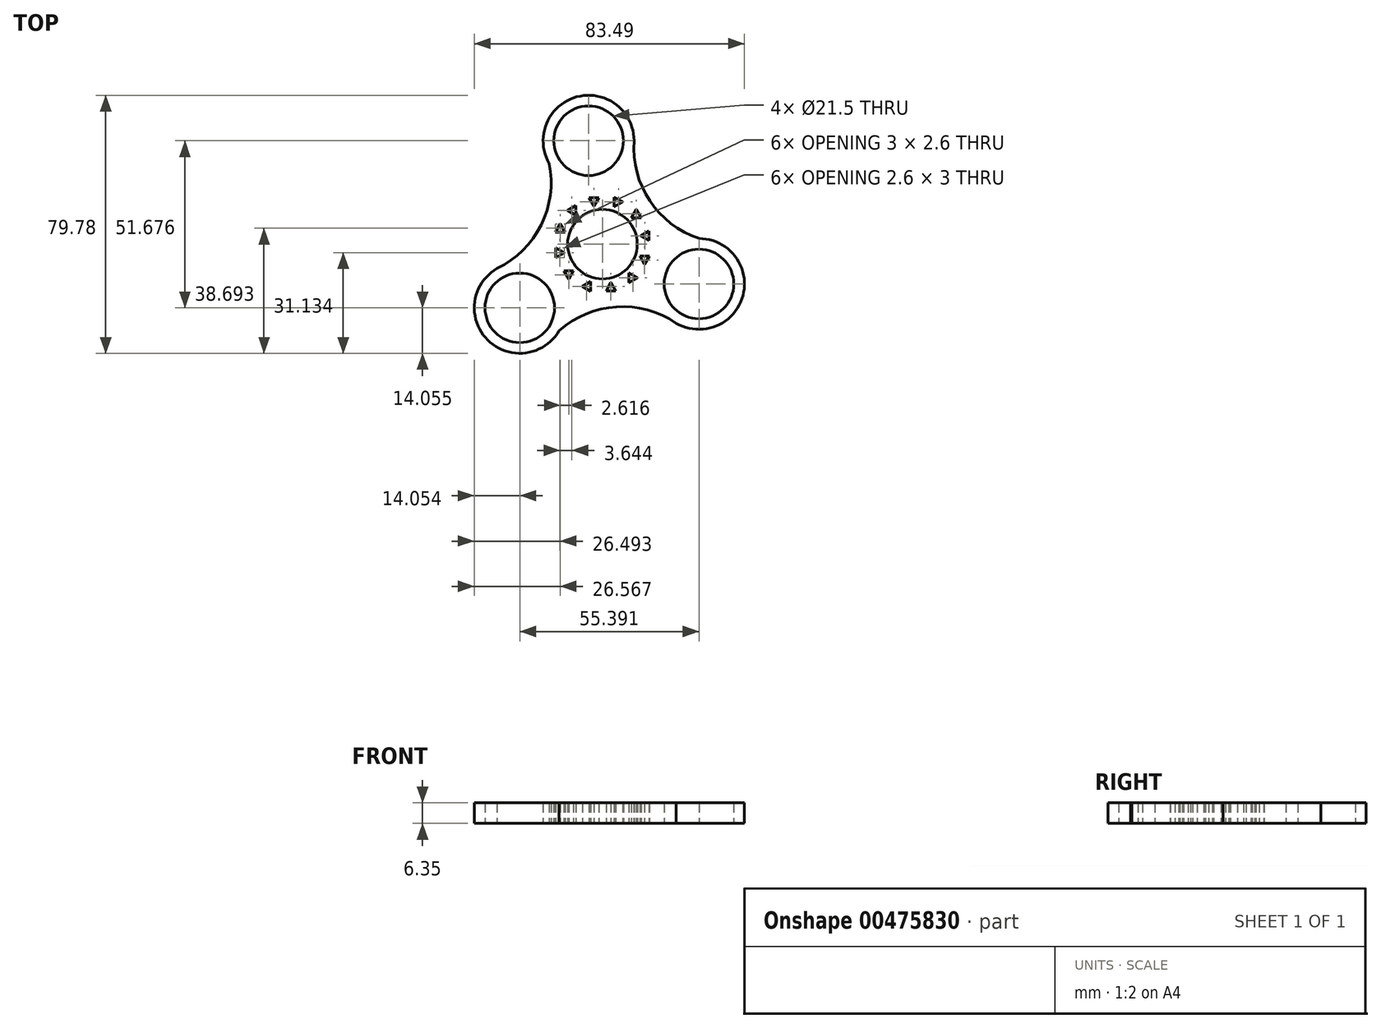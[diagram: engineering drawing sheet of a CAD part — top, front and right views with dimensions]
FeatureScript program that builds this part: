
annotation { "Feature Type Name" : "Feature", "Feature Type Description" : "" }
export const myFeature = defineFeature(function(context is Context, id is Id, definition is map)
    precondition{}
    {
        {
            var Q0;
            Q0=qCreatedBy(makeId("Top.planeOp"),FACE);
            var sketch = newSketch(context, id + "F0", { "sketchPlane" : qUnion([Q0])});
            skCircle(sketch, "E0", {"center": v(0, 0) * mm, "radius": 10.75 * mm});
            skArc(sketch, "E1", {"start": v(-31.32, -6.88) * mm, "mid": v(-35.98, -29.12) * mm, "end": v(-13.39, -26.72) * mm});
            skCircle(sketch, "E2", {"center": v(-25.56, -19.7) * mm, "radius": 10.75 * mm});
            skArc(sketch, "E3.1.2", {"start": v(21.62, -23.68) * mm, "mid": v(43.2, -16.6) * mm, "end": v(29.83, 1.77) * mm});
            skCircle(sketch, "E3.1.3", {"center": v(29.83, -12.28) * mm, "radius": 10.75 * mm});
            skArc(sketch, "E3.2.2", {"start": v(9.7, 30.56) * mm, "mid": v(-7.22, 45.72) * mm, "end": v(-16.45, 24.96) * mm});
            skCircle(sketch, "E3.2.3", {"center": v(-4.28, 31.98) * mm, "radius": 10.75 * mm});
            skArc(sketch, "E4", {"start": v(9.77, 31.98) * mm, "mid": v(14.62, 13.43) * mm, "end": v(29.83, 1.77) * mm});
            skArc(sketch, "E5.1.0", {"start": v(-32.58, -7.53) * mm, "mid": v(-18.94, 5.95) * mm, "end": v(-16.45, 24.96) * mm});
            skArc(sketch, "E5.2.0", {"start": v(22.8, -24.45) * mm, "mid": v(4.32, -19.38) * mm, "end": v(-13.39, -26.72) * mm});
            skLineSegment(sketch, "E6", {"start": v(-15.18, -6.28) * mm, "end": v(-10.43, -2.62) * mm});
            skLineSegment(sketch, "E7.MirrorCS", {"start": v(-9.8, -13.27) * mm, "end": v(-5.04, -9.6) * mm});
            skLineSegment(sketch, "E8.1.0", {"start": v(19.09, -12.43) * mm, "end": v(19.08, -12.43) * mm});
            skLineSegment(sketch, "E8.1.1", {"start": v(22.6, -4.34) * mm, "end": v(22.44, -4.28) * mm});
            skLineSegment(sketch, "E8.2.0", {"start": v(1.67, 23.03) * mm, "end": v(1.73, 22.6) * mm});
            skLineSegment(sketch, "E8.2.1", {"start": v(-7.04, 21.6) * mm, "end": v(-7.02, 21.43) * mm});
            skPoint(sketch, "E8.center", {"position": v(0.3, 0.07) * mm});
            skArc(sketch, "E9", {"start": v(-15.18, -6.28) * mm, "mid": v(-12.99, -10.16) * mm, "end": v(-9.8, -13.27) * mm});
            skArc(sketch, "E10.1.0", {"start": v(13.53, -10.15) * mm, "mid": v(15.8, -6.31) * mm, "end": v(16.9, -2) * mm});
            skArc(sketch, "E10.2.0", {"start": v(2.52, 16.65) * mm, "mid": v(-1.93, 16.7) * mm, "end": v(-6.22, 15.48) * mm});
            skLineSegment(sketch, "E11.trimOffspring", {"start": v(16.9, -2) * mm, "end": v(11.34, 0.3) * mm});
            skLineSegment(sketch, "E12.trimOffspring", {"start": v(13.53, -10.15) * mm, "end": v(7.98, -7.86) * mm});
            skLineSegment(sketch, "E13.trimOffspring", {"start": v(2.52, 16.65) * mm, "end": v(3.32, 10.7) * mm});
            skLineSegment(sketch, "E14.trimOffspring", {"start": v(-6.22, 15.48) * mm, "end": v(-5.42, 9.53) * mm});
            skLineSegment(sketch, "E15", {"start": v(-14.54, 3.64) * mm, "end": v(-13.04, 6.24) * mm});
            skLineSegment(sketch, "E16", {"start": v(-13.04, 6.24) * mm, "end": v(-11.54, 3.64) * mm});
            skLineSegment(sketch, "E17", {"start": v(-11.54, 3.64) * mm, "end": v(-14.54, 3.64) * mm});
            skLineSegment(sketch, "E18.1.0", {"start": v(-14.42, -4.12) * mm, "end": v(-14.42, -1.12) * mm});
            skLineSegment(sketch, "E18.1.1", {"start": v(-14.42, -1.12) * mm, "end": v(-11.82, -2.62) * mm});
            skLineSegment(sketch, "E18.1.2", {"start": v(-11.82, -2.62) * mm, "end": v(-14.42, -4.12) * mm});
            skLineSegment(sketch, "E18.2.0", {"start": v(-10.43, -10.77) * mm, "end": v(-11.93, -8.17) * mm});
            skLineSegment(sketch, "E18.2.1", {"start": v(-11.93, -8.17) * mm, "end": v(-8.93, -8.17) * mm});
            skLineSegment(sketch, "E18.2.2", {"start": v(-8.93, -8.17) * mm, "end": v(-10.43, -10.77) * mm});
            skLineSegment(sketch, "E19.1.3.0", {"start": v(-3.64, -14.54) * mm, "end": v(-6.24, -13.04) * mm});
            skLineSegment(sketch, "E19.3.3.0", {"start": v(-6.24, -13.04) * mm, "end": v(-3.64, -11.54) * mm});
            skLineSegment(sketch, "E19.6.3.0", {"start": v(-3.64, -11.54) * mm, "end": v(-3.64, -14.54) * mm});
            skLineSegment(sketch, "E19.1.4.0", {"start": v(4.12, -14.42) * mm, "end": v(1.12, -14.42) * mm});
            skLineSegment(sketch, "E19.3.4.0", {"start": v(1.12, -14.42) * mm, "end": v(2.62, -11.82) * mm});
            skLineSegment(sketch, "E19.6.4.0", {"start": v(2.62, -11.82) * mm, "end": v(4.12, -14.42) * mm});
            skLineSegment(sketch, "E19.1.5.0", {"start": v(10.77, -10.43) * mm, "end": v(8.17, -11.93) * mm});
            skLineSegment(sketch, "E19.3.5.0", {"start": v(8.17, -11.93) * mm, "end": v(8.17, -8.93) * mm});
            skLineSegment(sketch, "E19.6.5.0", {"start": v(8.17, -8.93) * mm, "end": v(10.77, -10.43) * mm});
            skLineSegment(sketch, "E20.1.6.0", {"start": v(14.54, -3.64) * mm, "end": v(13.04, -6.24) * mm});
            skLineSegment(sketch, "E20.3.6.0", {"start": v(13.04, -6.24) * mm, "end": v(11.54, -3.64) * mm});
            skLineSegment(sketch, "E20.6.6.0", {"start": v(11.54, -3.64) * mm, "end": v(14.54, -3.64) * mm});
            skLineSegment(sketch, "E20.1.7.0", {"start": v(14.42, 4.12) * mm, "end": v(14.42, 1.12) * mm});
            skLineSegment(sketch, "E20.3.7.0", {"start": v(14.42, 1.12) * mm, "end": v(11.82, 2.62) * mm});
            skLineSegment(sketch, "E20.6.7.0", {"start": v(11.82, 2.62) * mm, "end": v(14.42, 4.12) * mm});
            skLineSegment(sketch, "E20.1.8.0", {"start": v(10.43, 10.77) * mm, "end": v(11.93, 8.17) * mm});
            skLineSegment(sketch, "E20.3.8.0", {"start": v(11.93, 8.17) * mm, "end": v(8.93, 8.17) * mm});
            skLineSegment(sketch, "E20.6.8.0", {"start": v(8.93, 8.17) * mm, "end": v(10.43, 10.77) * mm});
            skLineSegment(sketch, "E20.1.9.0", {"start": v(3.64, 14.54) * mm, "end": v(6.24, 13.04) * mm});
            skLineSegment(sketch, "E20.3.9.0", {"start": v(6.24, 13.04) * mm, "end": v(3.64, 11.54) * mm});
            skLineSegment(sketch, "E20.6.9.0", {"start": v(3.64, 11.54) * mm, "end": v(3.64, 14.54) * mm});
            skLineSegment(sketch, "E20.1.10.0", {"start": v(-4.12, 14.42) * mm, "end": v(-1.12, 14.42) * mm});
            skLineSegment(sketch, "E20.3.10.0", {"start": v(-1.12, 14.42) * mm, "end": v(-2.62, 11.82) * mm});
            skLineSegment(sketch, "E20.6.10.0", {"start": v(-2.62, 11.82) * mm, "end": v(-4.12, 14.42) * mm});
            skLineSegment(sketch, "E20.1.11.0", {"start": v(-10.77, 10.43) * mm, "end": v(-8.17, 11.93) * mm});
            skLineSegment(sketch, "E20.3.11.0", {"start": v(-8.17, 11.93) * mm, "end": v(-8.17, 8.93) * mm});
            skLineSegment(sketch, "E20.6.11.0", {"start": v(-8.17, 8.93) * mm, "end": v(-10.77, 10.43) * mm});
            skSolve(sketch);
        }
        {
            var Q0;
            Q0=makeQuery(id+"F0.imprint","IMPRINT",FACE,{"disambiguationData":[TD([[makeQuery(id+"F0.imprint","IMPRINT",EDGE,{"derivedFrom":sQuery(id+"F0.wireOp",EDGE,"E2")}),-1.0]])]});
            extrude(context, id + "F1", {"entities" : qUnion([Q0]), "depth" : 6.35 * mm});
        }
    });
